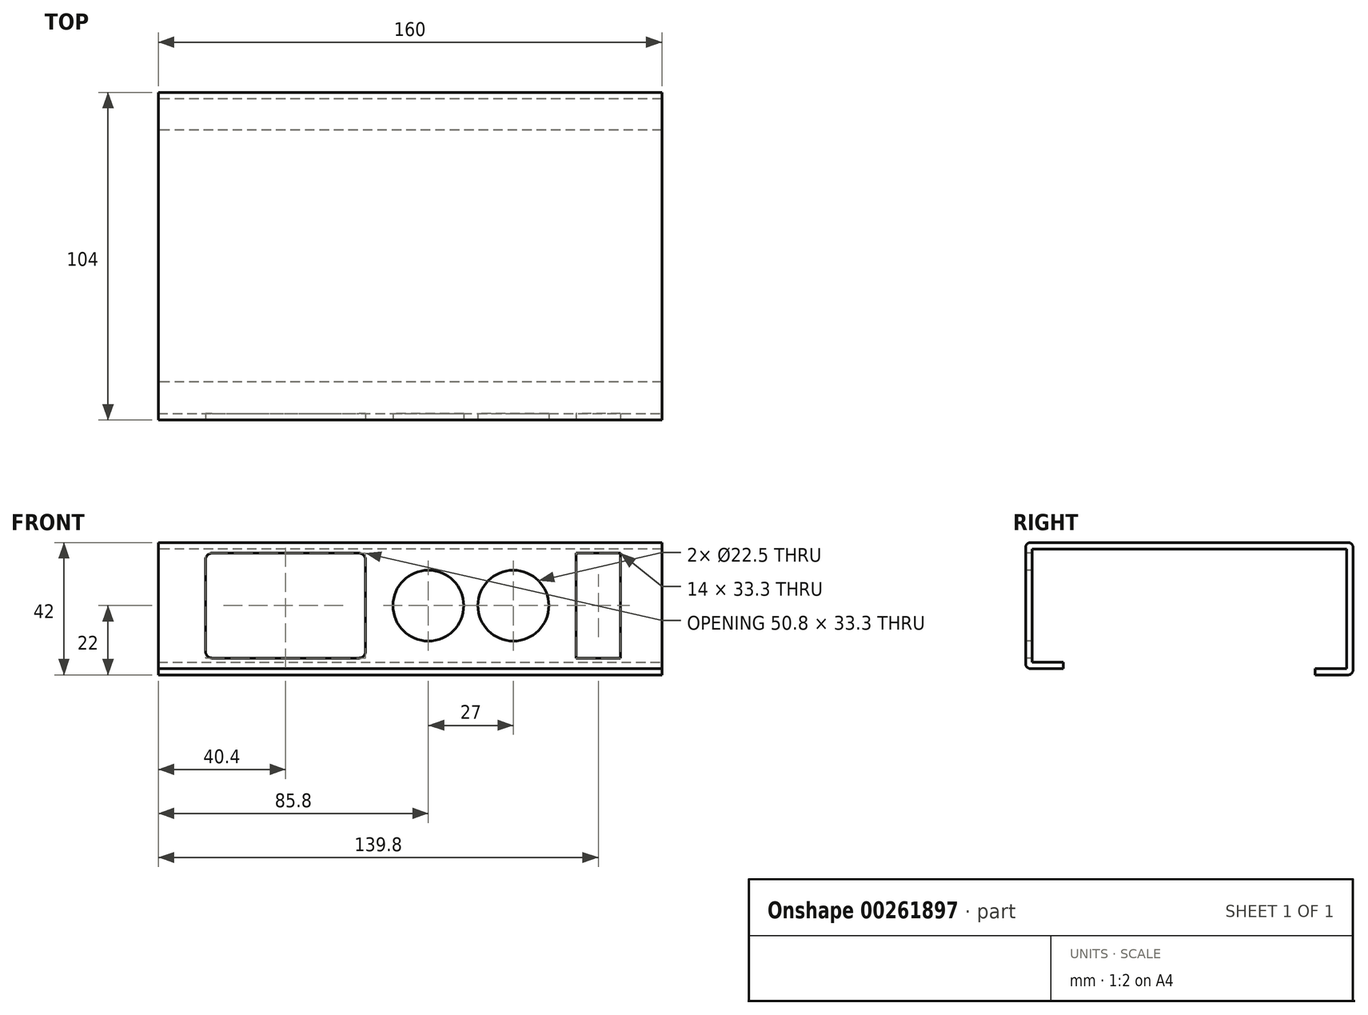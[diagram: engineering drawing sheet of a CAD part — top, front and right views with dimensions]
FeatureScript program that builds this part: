
annotation { "Feature Type Name" : "Feature", "Feature Type Description" : "" }
export const myFeature = defineFeature(function(context is Context, id is Id, definition is map)
    precondition{}
    {
        {
            var Q0;
            Q0=qCreatedBy(makeId("Front.planeOp"),FACE);
            var sketch = newSketch(context, id + "F0", { "sketchPlane" : qUnion([Q0])});
            skLineSegment(sketch, "E0.bottom", {"start": v(0, 0) * mm, "end": v(-160, 0) * mm});
            skLineSegment(sketch, "E0.top", {"start": v(0, 40) * mm, "end": v(-160, 40) * mm});
            skLineSegment(sketch, "E0.left", {"start": v(0, 0) * mm, "end": v(0, 40) * mm});
            skLineSegment(sketch, "E0.right", {"start": v(-160, 0) * mm, "end": v(-160, 40) * mm});
            skSolve(sketch);
        }
        {
            var Q0;
            Q0 = qSketchRegion(id + "F0", true);
            extrude(context, id + "F1", {"entities" : qUnion([Q0]), "depth" : 2 * mm});
        }
        {
            var Q0;
            Q0=makeQuery(id+"F1.opExtrude","CAP_FACE",FACE,{"disambiguationData":[OSD([sQuery(id+"F0.wireOp",EDGE,"E0.bottom"),sQuery(id+"F0.wireOp",EDGE,"E0.top"),sQuery(id+"F0.wireOp",EDGE,"E0.left"),sQuery(id+"F0.wireOp",EDGE,"E0.right")])],"isStart":false});
            var sketch = newSketch(context, id + "F2", { "sketchPlane" : qUnion([Q0])});
            skLineSegment(sketch, "E1.bottom", {"start": v(-143, 36.65) * mm, "end": v(-96.2, 36.65) * mm});
            skLineSegment(sketch, "E1.top", {"start": v(-143, 3.35) * mm, "end": v(-96.2, 3.35) * mm});
            skLineSegment(sketch, "E1.left", {"start": v(-145, 34.65) * mm, "end": v(-145, 5.35) * mm});
            skLineSegment(sketch, "E1.right", {"start": v(-94.2, 34.65) * mm, "end": v(-94.2, 5.35) * mm});
            skPoint(sketch, "E2.visualSharp", {"position": v(-145, 36.65) * mm});
            skArc(sketch, "E2.filletArc", {"start": v(-143, 36.65) * mm, "mid": v(-144.41, 36.06) * mm, "end": v(-145, 34.65) * mm});
            skPoint(sketch, "E3.visualSharp", {"position": v(-94.2, 36.65) * mm});
            skArc(sketch, "E3.filletArc", {"start": v(-94.2, 34.65) * mm, "mid": v(-94.79, 36.06) * mm, "end": v(-96.2, 36.65) * mm});
            skPoint(sketch, "E4.visualSharp", {"position": v(-94.2, 3.35) * mm});
            skArc(sketch, "E4.filletArc", {"start": v(-96.2, 3.35) * mm, "mid": v(-94.79, 3.94) * mm, "end": v(-94.2, 5.35) * mm});
            skPoint(sketch, "E5.visualSharp", {"position": v(-145, 3.35) * mm});
            skArc(sketch, "E5.filletArc", {"start": v(-145, 5.35) * mm, "mid": v(-144.41, 3.94) * mm, "end": v(-143, 3.35) * mm});
            skCircle(sketch, "E6", {"center": v(-74.2, 20) * mm, "radius": 11.25 * mm});
            skCircle(sketch, "E7", {"center": v(-47.2, 20) * mm, "radius": 11.25 * mm});
            skLineSegment(sketch, "E8.bottom", {"start": v(-13.2, 36.65) * mm, "end": v(-27.2, 36.65) * mm});
            skLineSegment(sketch, "E8.top", {"start": v(-13.2, 3.35) * mm, "end": v(-27.2, 3.35) * mm});
            skLineSegment(sketch, "E8.left", {"start": v(-13.2, 36.65) * mm, "end": v(-13.2, 3.35) * mm});
            skLineSegment(sketch, "E8.right", {"start": v(-27.2, 36.65) * mm, "end": v(-27.2, 3.35) * mm});
            skSolve(sketch);
        }
        {
            var Q0;
            Q0=makeQuery(id+"F2.imprint","IMPRINT",FACE,{"disambiguationData":[TD([[makeQuery(id+"F2.imprint","IMPRINT",EDGE,{"derivedFrom":sQuery(id+"F2.wireOp",EDGE,"E1.bottom")}),-1.0]])]});
            var Q1;
            Q1=makeQuery(id+"F2.imprint","IMPRINT",FACE,{"disambiguationData":[TD([[makeQuery(id+"F2.imprint","IMPRINT",EDGE,{"derivedFrom":sQuery(id+"F2.wireOp",EDGE,"E6")}),1.0]])]});
            var Q2;
            Q2=makeQuery(id+"F2.imprint","IMPRINT",FACE,{"disambiguationData":[TD([[makeQuery(id+"F2.imprint","IMPRINT",EDGE,{"derivedFrom":sQuery(id+"F2.wireOp",EDGE,"E7")}),1.0]])]});
            var Q3;
            Q3=makeQuery(id+"F2.imprint","IMPRINT",FACE,{"disambiguationData":[TD([[makeQuery(id+"F2.imprint","IMPRINT",EDGE,{"derivedFrom":sQuery(id+"F2.wireOp",EDGE,"E8.bottom")}),1.0]])]});
            extrude(context, id + "F3", {"entities" : qUnion([Q0, Q1, Q2, Q3]), "operationType" : NewBodyOperationType.REMOVE, "oppositeDirection" : true, "depth" : 10 * mm});
        }
        {
            var Q0;
            Q0=makeQuery(id+"F1.opExtrude","CAP_FACE",FACE,{"disambiguationData":[OSD([sQuery(id+"F0.wireOp",EDGE,"E0.bottom"),sQuery(id+"F0.wireOp",EDGE,"E0.top"),sQuery(id+"F0.wireOp",EDGE,"E0.left"),sQuery(id+"F0.wireOp",EDGE,"E0.right")])],"isStart":true});
            var sketch = newSketch(context, id + "F4", { "sketchPlane" : qUnion([Q0])});
            skLineSegment(sketch, "E9.bottom", {"start": v(0, 40) * mm, "end": v(160, 40) * mm});
            skLineSegment(sketch, "E9.top", {"start": v(0, 38) * mm, "end": v(160, 38) * mm});
            skLineSegment(sketch, "E9.left", {"start": v(0, 40) * mm, "end": v(0, 38) * mm});
            skLineSegment(sketch, "E9.right", {"start": v(160, 40) * mm, "end": v(160, 38) * mm});
            skSolve(sketch);
        }
        {
            var Q0;
            Q0=makeQuery(id+"F4.imprint","IMPRINT",FACE,{"disambiguationData":[TD([[makeQuery(id+"F4.imprint","IMPRINT",EDGE,{"derivedFrom":sQuery(id+"F4.wireOp",EDGE,"E9.bottom")}),-1.0]])]});
            extrude(context, id + "F5", {"entities" : qUnion([Q0]), "operationType" : NewBodyOperationType.ADD, "depth" : 102 * mm});
        }
        {
            var Q0;
            Q0=makeQuery(id+"F5.opExtrude","SWEPT_FACE",FACE,{"disambiguationData":[OSD([sQuery(id+"F4.wireOp",EDGE,"E9.top")])]});
            var sketch = newSketch(context, id + "F6", { "sketchPlane" : qUnion([Q0])});
            skLineSegment(sketch, "E10.bottom", {"start": v(0, -102) * mm, "end": v(-160, -102) * mm});
            skLineSegment(sketch, "E10.top", {"start": v(0, -100) * mm, "end": v(-160, -100) * mm});
            skLineSegment(sketch, "E10.left", {"start": v(0, -102) * mm, "end": v(0, -100) * mm});
            skLineSegment(sketch, "E10.right", {"start": v(-160, -102) * mm, "end": v(-160, -100) * mm});
            skSolve(sketch);
        }
        {
            var Q0;
            Q0=makeQuery(id+"F6.imprint","IMPRINT",FACE,{"disambiguationData":[TD([[makeQuery(id+"F6.imprint","IMPRINT",EDGE,{"derivedFrom":sQuery(id+"F6.wireOp",EDGE,"E10.bottom")}),-1.0]])]});
            extrude(context, id + "F7", {"entities" : qUnion([Q0]), "operationType" : NewBodyOperationType.ADD, "depth" : 40 * mm});
        }
        {
            var Q0;
            Q0=makeQuery(id+"F1.opExtrude","CAP_FACE",FACE,{"disambiguationData":[OSD([sQuery(id+"F0.wireOp",EDGE,"E0.bottom"),sQuery(id+"F0.wireOp",EDGE,"E0.top"),sQuery(id+"F0.wireOp",EDGE,"E0.left"),sQuery(id+"F0.wireOp",EDGE,"E0.right")])],"isStart":true});
            var sketch = newSketch(context, id + "F8", { "sketchPlane" : qUnion([Q0])});
            skLineSegment(sketch, "E11.bottom", {"start": v(160, 0) * mm, "end": v(0, 0) * mm});
            skLineSegment(sketch, "E11.top", {"start": v(160, 2) * mm, "end": v(0, 2) * mm});
            skLineSegment(sketch, "E11.left", {"start": v(160, 0) * mm, "end": v(160, 2) * mm});
            skLineSegment(sketch, "E11.right", {"start": v(0, 0) * mm, "end": v(0, 2) * mm});
            skSolve(sketch);
        }
        {
            var Q0;
            Q0=makeQuery(id+"F7.opExtrude","SWEPT_FACE",FACE,{"disambiguationData":[OSD([sQuery(id+"F6.wireOp",EDGE,"E10.top")])]});
            var sketch = newSketch(context, id + "F9", { "sketchPlane" : qUnion([Q0])});
            skLineSegment(sketch, "E12.bottom", {"start": v(0, -2) * mm, "end": v(-160, -2) * mm});
            skLineSegment(sketch, "E12.top", {"start": v(0, 0) * mm, "end": v(-160, 0) * mm});
            skLineSegment(sketch, "E12.left", {"start": v(0, -2) * mm, "end": v(0, 0) * mm});
            skLineSegment(sketch, "E12.right", {"start": v(-160, -2) * mm, "end": v(-160, 0) * mm});
            skSolve(sketch);
        }
        {
            var Q0;
            Q0=makeQuery(id+"F8.imprint","IMPRINT",FACE,{"disambiguationData":[TD([[makeQuery(id+"F8.imprint","IMPRINT",EDGE,{"derivedFrom":sQuery(id+"F8.wireOp",EDGE,"E11.bottom")}),1.0]])]});
            extrude(context, id + "F10", {"entities" : qUnion([Q0]), "operationType" : NewBodyOperationType.ADD, "depth" : 10 * mm});
        }
        {
            var Q0;
            Q0=makeQuery(id+"F9.imprint","IMPRINT",FACE,{"disambiguationData":[TD([[makeQuery(id+"F9.imprint","IMPRINT",EDGE,{"derivedFrom":sQuery(id+"F9.wireOp",EDGE,"E12.bottom")}),-1.0]])]});
            extrude(context, id + "F11", {"entities" : qUnion([Q0]), "operationType" : NewBodyOperationType.ADD, "depth" : 10 * mm});
        }
        {
            var Q0;
            Q0=makeQuery(id+"F1.opExtrude","CAP_EDGE",EDGE,{"disambiguationData":[OSD([sQuery(id+"F0.wireOp",EDGE,"E0.top")])],"isStart":false});
            var Q1;
            Q1=makeQuery(id+"F1.opExtrude","CAP_EDGE",EDGE,{"disambiguationData":[OSD([sQuery(id+"F0.wireOp",EDGE,"E0.bottom")])],"isStart":false});
            var Q2;
            Q2=makeQuery(id+"F5.opExtrude","CAP_EDGE",EDGE,{"disambiguationData":[OSD([sQuery(id+"F4.wireOp",EDGE,"E9.bottom")])],"isStart":false});
            var Q3;
            Q3=makeQuery(id+"F7.opExtrude","CAP_EDGE",EDGE,{"disambiguationData":[OSD([sQuery(id+"F6.wireOp",EDGE,"E10.bottom")])],"isStart":false});
            var Q4;
            Q4=makeQuery(id+"F5.opExtrude","CAP_EDGE",EDGE,{"disambiguationData":[OSD([sQuery(id+"F4.wireOp",EDGE,"E9.top")])],"isStart":true});
            var Q5;
            Q5=makeQuery(id+"F10.opExtrude","CAP_EDGE",EDGE,{"disambiguationData":[OSD([sQuery(id+"F8.wireOp",EDGE,"E11.top")])],"isStart":true});
            var Q6;
            Q6=makeQuery(id+"F7.opExtrude","CAP_EDGE",EDGE,{"disambiguationData":[OSD([sQuery(id+"F6.wireOp",EDGE,"E10.top")])],"isStart":true});
            var Q7;
            Q7=makeQuery(id+"F11.opExtrude","CAP_EDGE",EDGE,{"disambiguationData":[OSD([sQuery(id+"F9.wireOp",EDGE,"E12.top")])],"isStart":true});
            fillet(context, id + "F12", {"entities" : qUnion([Q0, Q1, Q2, Q3, Q4, Q5, Q6, Q7]), "radius" : 1.5 * mm, "tangentPropagation" : true, "allowEdgeOverflow" : false});
        }
    });
